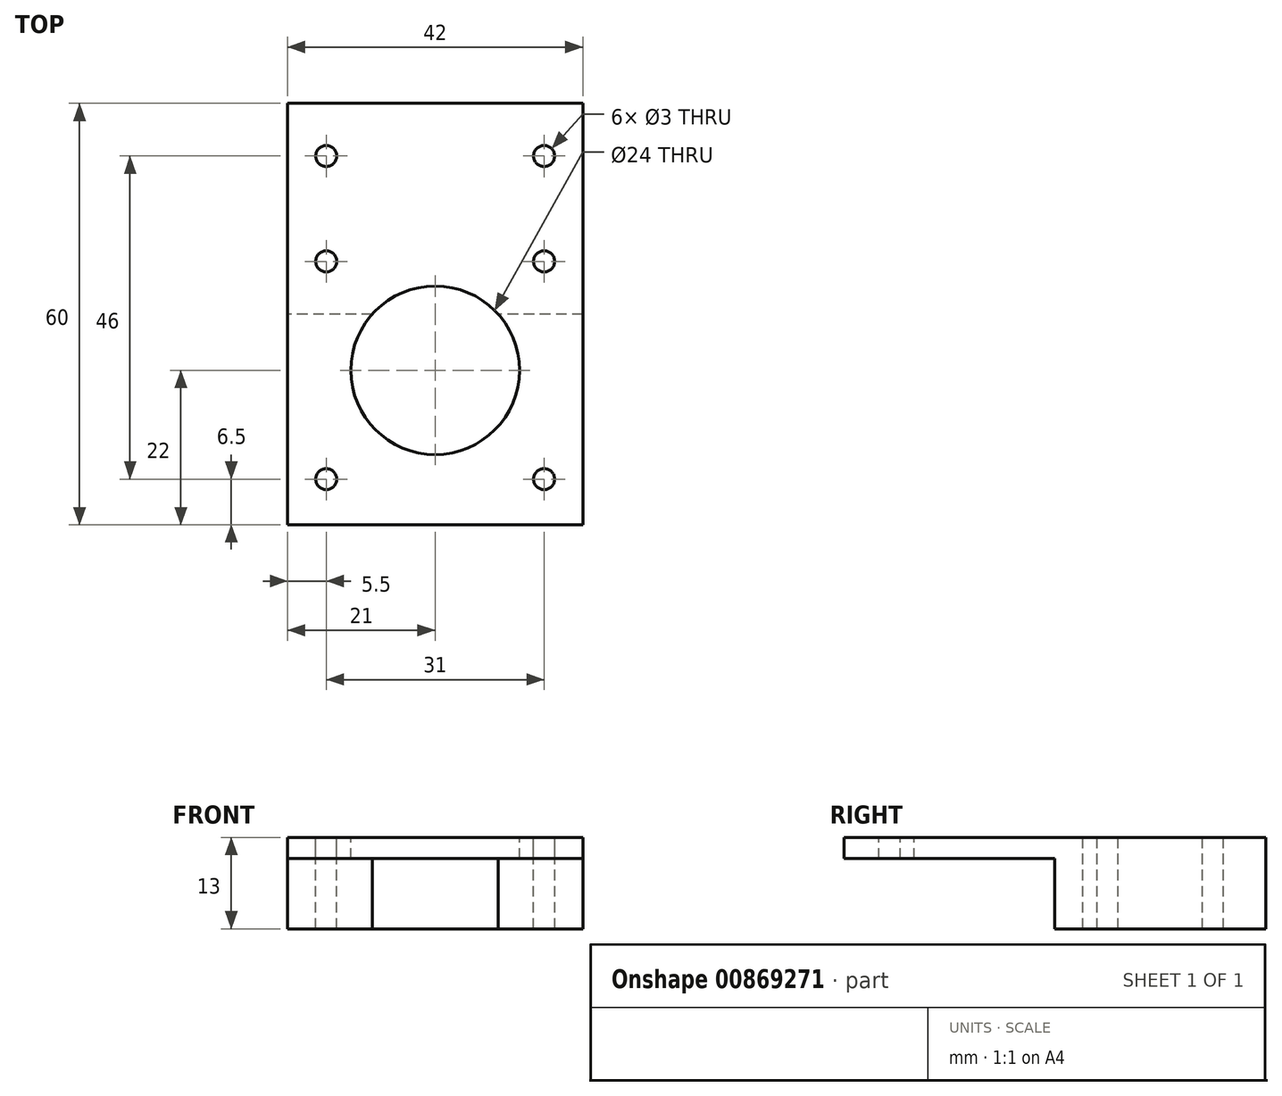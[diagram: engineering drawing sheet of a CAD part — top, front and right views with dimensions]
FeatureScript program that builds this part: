
annotation { "Feature Type Name" : "Feature", "Feature Type Description" : "" }
export const myFeature = defineFeature(function(context is Context, id is Id, definition is map)
    precondition{}
    {
        {
            var Q0;
            Q0=qCreatedBy(makeId("Top.planeOp"),FACE);
            var sketch = newSketch(context, id + "F0", { "sketchPlane" : qUnion([Q0])});
            skLineSegment(sketch, "E0.bottom", {"start": v(21, -15) * mm, "end": v(-21, -15) * mm});
            skLineSegment(sketch, "E0.top", {"start": v(21, 15) * mm, "end": v(-21, 15) * mm});
            skLineSegment(sketch, "E0.left", {"start": v(21, -15) * mm, "end": v(21, 15) * mm});
            skLineSegment(sketch, "E0.right", {"start": v(-21, -15) * mm, "end": v(-21, 15) * mm});
            skPoint(sketch, "E0.middle", {"position": v(0, 0) * mm});
            skSolve(sketch);
        }
        {
            var Q0;
            Q0=qSketchRegion(id+"F0",true);
            extrude(context, id + "F1", {"entities" : qUnion([Q0]), "depth" : 10 * mm, "offsetDistance" : 25 * mm});
        }
        {
            var Q0;
            Q0=makeQuery(id+"F1.opExtrude","CAP_FACE",FACE,{"disambiguationData":[OSD([sQuery(id+"F0.wireOp",EDGE,"E0.bottom"),sQuery(id+"F0.wireOp",EDGE,"E0.top"),sQuery(id+"F0.wireOp",EDGE,"E0.left"),sQuery(id+"F0.wireOp",EDGE,"E0.right")])],"isStart":false});
            extrude(context, id + "F2", {"entities" : qUnion([Q0]), "depth" : 3 * mm, "offsetDistance" : 25 * mm});
        }
        {
            var Q0;
            Q0=makeQuery(id+"F2.opExtrude","SWEPT_FACE",FACE,{"disambiguationData":[OSD([sQuery(id+"F0.wireOp",EDGE,"E0.bottom")])]});
            extrude(context, id + "F3", {"entities" : qUnion([Q0]), "operationType" : NewBodyOperationType.ADD, "depth" : 30 * mm, "offsetDistance" : 25 * mm});
        }
        {
            var Q0;
            {var subQ0=sQuery(id+"F0.wireOp",EDGE,"E0.bottom");Q0=makeQuery(id+"F3.boolean.opBoolean","MERGE",FACE,{"derivedFrom":[makeQuery(id+"F2.opExtrude","CAP_FACE",FACE,{"disambiguationData":[OSD([subQ0,sQuery(id+"F0.wireOp",EDGE,"E0.top"),sQuery(id+"F0.wireOp",EDGE,"E0.left"),sQuery(id+"F0.wireOp",EDGE,"E0.right")])],"isStart":false}),makeQuery(id+"F3.opExtrude","SWEPT_FACE",FACE,{"disambiguationData":[OSD([subQ0]),TDD([makeQuery(id+"F2.opExtrude","CAP_EDGE",EDGE,{"disambiguationData":[OSD([subQ0])],"isStart":false})])]})]});}
            var sketch = newSketch(context, id + "F4", { "sketchPlane" : qUnion([Q0])});
            skLineSegment(sketch, "E1.bottom", {"start": v(-15.5, -38.5) * mm, "end": v(15.5, -38.5) * mm});
            skLineSegment(sketch, "E1.top", {"start": v(-15.5, 7.5) * mm, "end": v(15.5, 7.5) * mm});
            skLineSegment(sketch, "E1.left", {"start": v(-15.5, -38.5) * mm, "end": v(-15.5, 7.5) * mm});
            skLineSegment(sketch, "E1.right", {"start": v(15.5, -38.5) * mm, "end": v(15.5, 7.5) * mm});
            skPoint(sketch, "E1.middle", {"position": v(0, -15.5) * mm});
            skLineSegment(sketch, "E2", {"start": v(15.5, -7.5) * mm, "end": v(-15.5, -7.5) * mm});
            skCircle(sketch, "E3", {"center": v(0, -23) * mm, "radius": 12 * mm});
            skPoint(sketch, "E3.centerSnap0", {"position": v(0, -38.5) * mm});
            skSolve(sketch);
        }
        {
            var Q0;
            Q0=sQuery(id+"F4.wireOp",VERTEX,"E2.end");
            var Q1;
            Q1=sQuery(id+"F4.wireOp",VERTEX,"E1.top.start");
            var Q2;
            Q2=sQuery(id+"F4.wireOp",VERTEX,"E1.top.end");
            var Q3;
            Q3=sQuery(id+"F4.wireOp",VERTEX,"E2.start");
            var Q4;
            Q4=sQuery(id+"F4.wireOp",VERTEX,"E1.bottom.end");
            var Q5;
            Q5=sQuery(id+"F4.wireOp",VERTEX,"E1.bottom.start");
            var Q6;
            Q6=makeQuery(id+"F2.opExtrude","SWEPT_BODY",BODY,{"disambiguationData":[OSD([sQuery(id+"F0.wireOp",EDGE,"E0.bottom"),sQuery(id+"F0.wireOp",EDGE,"E0.top"),sQuery(id+"F0.wireOp",EDGE,"E0.left"),sQuery(id+"F0.wireOp",EDGE,"E0.right")])]});
            var Q7;
            Q7=makeQuery(id+"F1.opExtrude","SWEPT_BODY",BODY,{"disambiguationData":[OSD([sQuery(id+"F0.wireOp",EDGE,"E0.bottom"),sQuery(id+"F0.wireOp",EDGE,"E0.top"),sQuery(id+"F0.wireOp",EDGE,"E0.left"),sQuery(id+"F0.wireOp",EDGE,"E0.right")])]});
            hole(context, id + "F5", {"style" : HoleStyle.SIMPLE, "endStyle" : HoleEndStyle.THROUGH, "holeDiameter" : 3 * mm, "majorDiameter" : 5 * mm, "isTappedThrough" : true, "tappedDepth" : 12 * mm, "tapClearance" : 3, "locations" : qUnion([Q0, Q1, Q2, Q3, Q4, Q5]), "scope" : qUnion([Q6, Q7])});
        }
        {
            var Q0;
            Q0=makeQuery(id+"F4.imprint","IMPRINT",FACE,{"disambiguationData":[TD([[makeQuery(id+"F4.imprint","IMPRINT",EDGE,{"derivedFrom":sQuery(id+"F4.wireOp",EDGE,"E3")}),1.0]])]});
            extrude(context, id + "F6", {"entities" : qUnion([Q0]), "operationType" : NewBodyOperationType.REMOVE, "oppositeDirection" : true, "depth" : 25 * mm, "offsetDistance" : 25 * mm});
        }
    });
